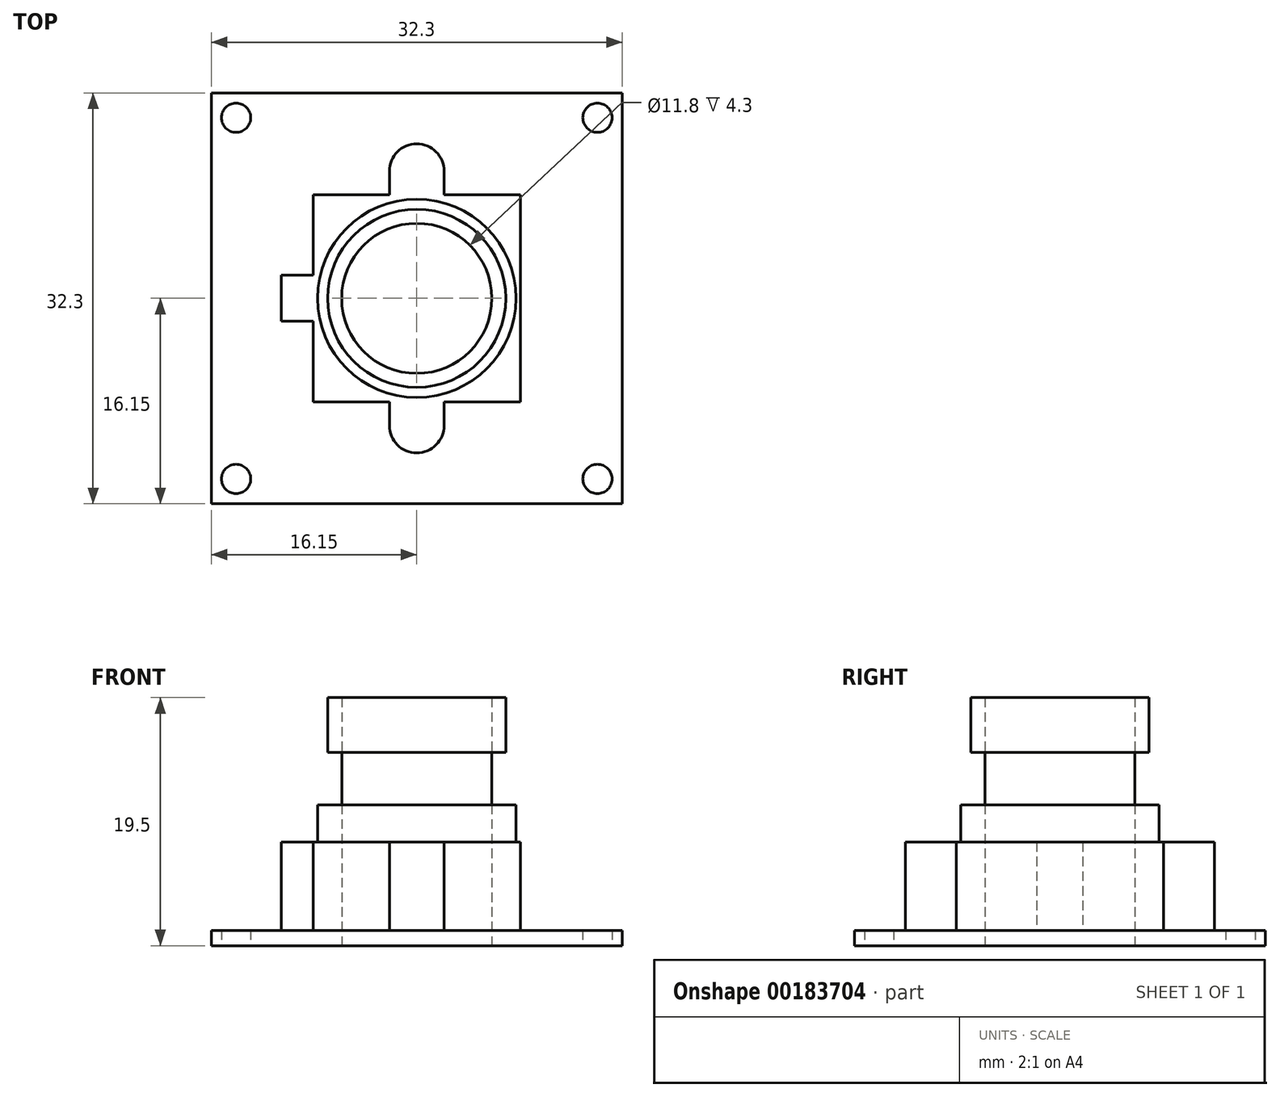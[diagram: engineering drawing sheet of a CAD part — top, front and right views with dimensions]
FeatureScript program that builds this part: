
annotation { "Feature Type Name" : "Feature", "Feature Type Description" : "" }
export const myFeature = defineFeature(function(context is Context, id is Id, definition is map)
    precondition{}
    {
        {
            var Q0;
            Q0=qCreatedBy(makeId("Top.planeOp"),FACE);
            var sketch = newSketch(context, id + "F0", { "sketchPlane" : qUnion([Q0])});
            skCircle(sketch, "E0", {"center": v(0, 0) * mm, "radius": 7.8 * mm});
            skLineSegment(sketch, "E1.bottom", {"start": v(-8.15, 8.15) * mm, "end": v(8.15, 8.15) * mm});
            skLineSegment(sketch, "E1.top", {"start": v(-8.15, -8.15) * mm, "end": v(8.15, -8.15) * mm});
            skLineSegment(sketch, "E1.left", {"start": v(-8.15, 8.15) * mm, "end": v(-8.15, -8.15) * mm});
            skLineSegment(sketch, "E1.right", {"start": v(8.15, 8.15) * mm, "end": v(8.15, -8.15) * mm});
            skLineSegment(sketch, "E2.bottom", {"start": v(-16.15, 16.15) * mm, "end": v(16.15, 16.15) * mm});
            skLineSegment(sketch, "E2.top", {"start": v(-16.15, -16.15) * mm, "end": v(16.15, -16.15) * mm});
            skLineSegment(sketch, "E2.left", {"start": v(-16.15, 16.15) * mm, "end": v(-16.15, -16.15) * mm});
            skLineSegment(sketch, "E2.right", {"start": v(16.15, 16.15) * mm, "end": v(16.15, -16.15) * mm});
            skCircle(sketch, "E3", {"center": v(0, 10) * mm, "radius": 2.15 * mm});
            skCircle(sketch, "E4", {"center": v(0, -10) * mm, "radius": 2.15 * mm});
            skCircle(sketch, "E5", {"center": v(-14.2, 14.2) * mm, "radius": 1.15 * mm});
            skCircle(sketch, "E6", {"center": v(14.2, 14.2) * mm, "radius": 1.15 * mm});
            skCircle(sketch, "E7", {"center": v(14.2, -14.2) * mm, "radius": 1.15 * mm});
            skCircle(sketch, "E8", {"center": v(-14.2, -14.2) * mm, "radius": 1.15 * mm});
            skLineSegment(sketch, "E9", {"start": v(2.15, 10) * mm, "end": v(2.15, 8.15) * mm});
            skLineSegment(sketch, "E10", {"start": v(-2.15, 10) * mm, "end": v(-2.15, 8.15) * mm});
            skLineSegment(sketch, "E11", {"start": v(2.15, -10) * mm, "end": v(2.15, -8.15) * mm});
            skLineSegment(sketch, "E12", {"start": v(-2.15, -10) * mm, "end": v(-2.15, -8.15) * mm});
            skPoint(sketch, "E13", {"position": v(-2.15, 8.15) * mm});
            skPoint(sketch, "E14", {"position": v(2.15, 8.15) * mm});
            skPoint(sketch, "E15", {"position": v(-2.15, 10) * mm});
            skPoint(sketch, "E16", {"position": v(2.15, 10) * mm});
            skPoint(sketch, "E17", {"position": v(-2.15, -8.15) * mm});
            skPoint(sketch, "E18", {"position": v(-2.15, -10) * mm});
            skPoint(sketch, "E19", {"position": v(2.15, -8.15) * mm});
            skPoint(sketch, "E20", {"position": v(2.15, -10) * mm});
            skLineSegment(sketch, "E21.bottom", {"start": v(-8.15, -1.81) * mm, "end": v(-10.65, -1.81) * mm});
            skLineSegment(sketch, "E21.top", {"start": v(-8.15, 1.81) * mm, "end": v(-10.65, 1.81) * mm});
            skLineSegment(sketch, "E21.left", {"start": v(-8.15, -1.81) * mm, "end": v(-8.15, 1.81) * mm});
            skLineSegment(sketch, "E21.right", {"start": v(-10.65, -1.81) * mm, "end": v(-10.65, 1.81) * mm});
            skSolve(sketch);
        }
        {
            var Q0;
            {var subQ0=sQuery(id+"F0.wireOp",EDGE,"E1.left");Q0=makeQuery(id+"F0.imprint","IMPRINT",FACE,{"disambiguationData":[TD([[makeQuery(id+"F0.imprint","IMPRINT",EDGE,{"derivedFrom":subQ0}),-1.0]])]});}
            extrude(context, id + "F1", {"entities" : qUnion([Q0]), "depth" : 1.2 * mm});
        }
        {
            var Q0;
            {var subQ0=sQuery(id+"F0.wireOp",EDGE,"E3");var subQ1=sQuery(id+"F0.wireOp",EDGE,"E1.bottom");var subQ2=makeQuery(id+"F0.imprint","INTERSECT",VERTEX,{"disambiguationData":[OD(0.0)],"derivedFrom":[subQ1,subQ0]});Q0=makeQuery(id+"F0.imprint","IMPRINT",FACE,{"disambiguationData":[TD([[makeQuery(id+"F0.imprint","IMPRINT",EDGE,{"disambiguationData":[TD([[subQ2,-1.0]])],"derivedFrom":subQ1}),-1.0]])]});}
            var Q1;
            {var subQ0=sQuery(id+"F0.wireOp",EDGE,"E4");var subQ1=sQuery(id+"F0.wireOp",EDGE,"E1.top");var subQ2=makeQuery(id+"F0.imprint","INTERSECT",VERTEX,{"disambiguationData":[OD(0.0)],"derivedFrom":[subQ1,subQ0]});Q1=makeQuery(id+"F0.imprint","IMPRINT",FACE,{"disambiguationData":[TD([[makeQuery(id+"F0.imprint","IMPRINT",EDGE,{"disambiguationData":[TD([[subQ2,-1.0]])],"derivedFrom":subQ1}),1.0]])]});}
            var Q2;
            {var subQ0=sQuery(id+"F0.wireOp",EDGE,"E12");Q2=makeQuery(id+"F0.imprint","IMPRINT",FACE,{"disambiguationData":[TD([[makeQuery(id+"F0.imprint","IMPRINT",EDGE,{"derivedFrom":subQ0}),-1.0]])]});}
            var Q3;
            {var subQ0=sQuery(id+"F0.wireOp",EDGE,"E11");Q3=makeQuery(id+"F0.imprint","IMPRINT",FACE,{"disambiguationData":[TD([[makeQuery(id+"F0.imprint","IMPRINT",EDGE,{"derivedFrom":subQ0}),1.0]])]});}
            var Q4;
            {var subQ0=sQuery(id+"F0.wireOp",EDGE,"E4");var subQ1=sQuery(id+"F0.wireOp",EDGE,"E1.top");var subQ2=makeQuery(id+"F0.imprint","INTERSECT",VERTEX,{"disambiguationData":[OD(0.0)],"derivedFrom":[subQ1,subQ0]});Q4=makeQuery(id+"F0.imprint","IMPRINT",FACE,{"disambiguationData":[TD([[makeQuery(id+"F0.imprint","IMPRINT",EDGE,{"disambiguationData":[TD([[subQ2,-1.0]])],"derivedFrom":subQ1}),-1.0]])]});}
            var Q5;
            {var subQ0=sQuery(id+"F0.wireOp",EDGE,"E9");Q5=makeQuery(id+"F0.imprint","IMPRINT",FACE,{"disambiguationData":[TD([[makeQuery(id+"F0.imprint","IMPRINT",EDGE,{"derivedFrom":subQ0}),-1.0]])]});}
            var Q6;
            {var subQ0=sQuery(id+"F0.wireOp",EDGE,"E10");Q6=makeQuery(id+"F0.imprint","IMPRINT",FACE,{"disambiguationData":[TD([[makeQuery(id+"F0.imprint","IMPRINT",EDGE,{"derivedFrom":subQ0}),1.0]])]});}
            var Q7;
            {var subQ0=sQuery(id+"F0.wireOp",EDGE,"E3");var subQ1=sQuery(id+"F0.wireOp",EDGE,"E1.bottom");var subQ2=makeQuery(id+"F0.imprint","INTERSECT",VERTEX,{"disambiguationData":[OD(0.0)],"derivedFrom":[subQ1,subQ0]});Q7=makeQuery(id+"F0.imprint","IMPRINT",FACE,{"disambiguationData":[TD([[makeQuery(id+"F0.imprint","IMPRINT",EDGE,{"disambiguationData":[TD([[subQ2,-1.0]])],"derivedFrom":subQ1}),1.0]])]});}
            var Q8;
            Q8=makeQuery(id+"F0.imprint","IMPRINT",FACE,{"disambiguationData":[TD([[makeQuery(id+"F0.imprint","IMPRINT",EDGE,{"derivedFrom":sQuery(id+"F0.wireOp",EDGE,"E0")}),-1.0]])]});
            var Q9;
            Q9=makeQuery(id+"F0.imprint","IMPRINT",FACE,{"disambiguationData":[TD([[makeQuery(id+"F0.imprint","IMPRINT",EDGE,{"derivedFrom":sQuery(id+"F0.wireOp",EDGE,"E21.bottom")}),-1.0]])]});
            extrude(context, id + "F2", {"entities" : qUnion([Q0, Q1, Q2, Q3, Q4, Q5, Q6, Q7, Q8, Q9]), "operationType" : NewBodyOperationType.ADD, "depth" : 8.14 * mm});
        }
        {
            var Q0;
            Q0=makeQuery(id+"F0.imprint","IMPRINT",FACE,{"disambiguationData":[TD([[makeQuery(id+"F0.imprint","IMPRINT",EDGE,{"derivedFrom":sQuery(id+"F0.wireOp",EDGE,"E0")}),1.0]])]});
            extrude(context, id + "F3", {"entities" : qUnion([Q0]), "operationType" : NewBodyOperationType.ADD, "depth" : 11.08 * mm});
        }
        {
            var Q0;
            Q0=qCreatedBy(makeId("Top.planeOp"),FACE);
            var sketch = newSketch(context, id + "F4", { "sketchPlane" : qUnion([Q0])});
            skCircle(sketch, "E22", {"center": v(0, 0) * mm, "radius": 7 * mm});
            skCircle(sketch, "E23", {"center": v(0, 0) * mm, "radius": 5.9 * mm});
            skSolve(sketch);
        }
        {
            var Q0;
            Q0=makeQuery(id+"F4.imprint","IMPRINT",FACE,{"disambiguationData":[TD([[makeQuery(id+"F4.imprint","IMPRINT",EDGE,{"derivedFrom":sQuery(id+"F4.wireOp",EDGE,"E23")}),1.0]])]});
            extrude(context, id + "F5", {"entities" : qUnion([Q0]), "depth" : 19.5 * mm});
        }
        {
            var Q0;
            Q0=makeQuery(id+"F4.imprint","IMPRINT",FACE,{"disambiguationData":[TD([[makeQuery(id+"F4.imprint","IMPRINT",EDGE,{"derivedFrom":sQuery(id+"F4.wireOp",EDGE,"E22")}),1.0]])]});
            extrude(context, id + "F6", {"entities" : qUnion([Q0]), "depth" : 19.5 * mm, "hasSecondDirection" : true, "secondDirectionOppositeDirection" : false, "secondDirectionDepth" : 15.2 * mm});
        }
    });
